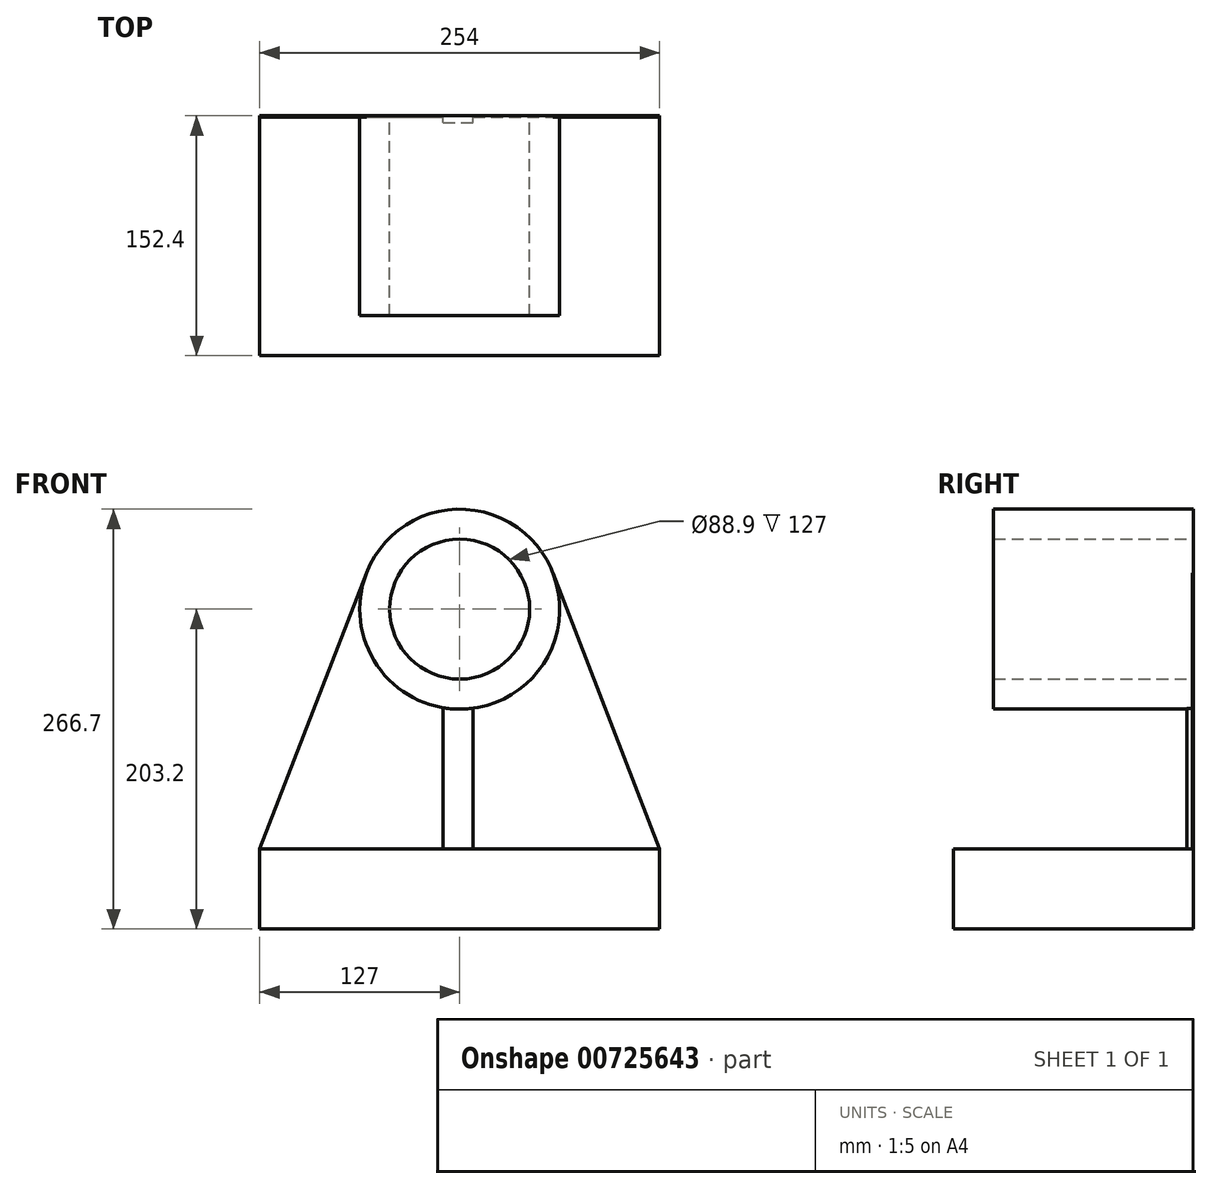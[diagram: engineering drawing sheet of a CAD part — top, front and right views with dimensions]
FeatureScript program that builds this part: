
annotation { "Feature Type Name" : "Feature", "Feature Type Description" : "" }
export const myFeature = defineFeature(function(context is Context, id is Id, definition is map)
    precondition{}
    {
        {
            assignVariable(context, id + "F0", {"name" : "C", "anyValue" : .75});
        }
        {
            var Q0;
            Q0=qCreatedBy(makeId("Front.planeOp"),FACE);
            var sketch = newSketch(context, id + "F1", { "sketchPlane" : qUnion([Q0])});
            skLineSegment(sketch, "E0.bottom", {"start": v(-127, 25.4) * mm, "end": v(127, 25.4) * mm});
            skLineSegment(sketch, "E0.top", {"start": v(-127, -25.4) * mm, "end": v(127, -25.4) * mm});
            skLineSegment(sketch, "E0.left", {"start": v(-127, 25.4) * mm, "end": v(-127, -25.4) * mm});
            skLineSegment(sketch, "E0.right", {"start": v(127, 25.4) * mm, "end": v(127, -25.4) * mm});
            skPoint(sketch, "E0.middle", {"position": v(0, 0) * mm});
            skPoint(sketch, "E1.endSnap0", {"position": v(0, 25.4) * mm});
            skCircle(sketch, "E2", {"center": v(0, 177.8) * mm, "radius": 63.5 * mm});
            skCircle(sketch, "E3.0", {"center": v(0, 177.8) * mm, "radius": 44.45 * mm});
            skLineSegment(sketch, "E4", {"start": v(-10.58, 115.19) * mm, "end": v(-10.58, 25.4) * mm});
            skLineSegment(sketch, "E5", {"start": v(8.47, 114.87) * mm, "end": v(8.47, 25.4) * mm});
            skPoint(sketch, "E6.start.orphan", {"position": v(0, 114.3) * mm});
            skLineSegment(sketch, "E7", {"start": v(-127, 25.4) * mm, "end": v(-59.23, 200.7) * mm});
            skLineSegment(sketch, "E8", {"start": v(127, 25.4) * mm, "end": v(59.23, 200.7) * mm});
            skSolve(sketch);
        }
        {
            var Q0;
            {var subQ0=sQuery(id+"F1.wireOp",EDGE,"E4");Q0=makeQuery(id+"F1.imprint","IMPRINT",FACE,{"disambiguationData":[TD([[makeQuery(id+"F1.imprint","IMPRINT",EDGE,{"derivedFrom":subQ0}),1.0]])]});}
            extrude(context, id + "F2", {"entities" : qUnion([Q0]), "depth" : (5 - getVariable(context, 'C')) * mm, "offsetDistance" : 25.4 * mm});
        }
        {
            var Q0;
            Q0=makeQuery(id+"F1.imprint","IMPRINT",FACE,{"disambiguationData":[TD([[makeQuery(id+"F1.imprint","IMPRINT",EDGE,{"derivedFrom":sQuery(id+"F1.wireOp",EDGE,"E0.top")}),1.0]])]});
            extrude(context, id + "F3", {"entities" : qUnion([Q0]), "operationType" : NewBodyOperationType.ADD, "depth" : 152.4 * mm, "offsetDistance" : 25.4 * mm});
        }
        {
            var Q0;
            {var subQ2=sQuery(id+"F1.wireOp",EDGE,"E4");Q0=makeQuery(id+"F1.imprint","IMPRINT",FACE,{"disambiguationData":[TD([[makeQuery(id+"F1.imprint","IMPRINT",EDGE,{"derivedFrom":subQ2}),-1.0]])]});}
            var Q1;
            {var subQ2=sQuery(id+"F1.wireOp",EDGE,"E5");Q1=makeQuery(id+"F1.imprint","IMPRINT",FACE,{"disambiguationData":[TD([[makeQuery(id+"F1.imprint","IMPRINT",EDGE,{"derivedFrom":subQ2}),1.0]])]});}
            extrude(context, id + "F4", {"entities" : qUnion([Q0, Q1]), "operationType" : NewBodyOperationType.ADD, "depth" : (getVariable(context, 'C')) * mm, "offsetDistance" : 25.4 * mm});
        }
        {
            var Q0;
            Q0=makeQuery(id+"F1.imprint","IMPRINT",FACE,{"disambiguationData":[TD([[makeQuery(id+"F1.imprint","IMPRINT",EDGE,{"derivedFrom":sQuery(id+"F1.wireOp",EDGE,"E3.0")}),-1.0]])]});
            extrude(context, id + "F5", {"entities" : qUnion([Q0]), "operationType" : NewBodyOperationType.ADD, "depth" : 127 * mm, "offsetDistance" : 25.4 * mm});
        }
    });
